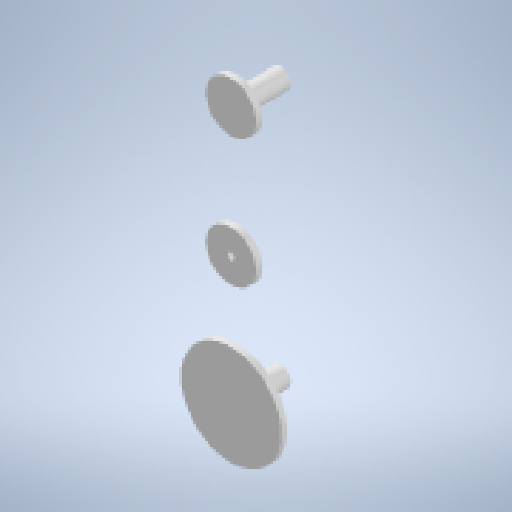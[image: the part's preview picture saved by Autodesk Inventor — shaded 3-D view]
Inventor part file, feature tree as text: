
AUTODESK INVENTOR PART (.ipt)
format: ipt  version: 2023 (Build 270158000, 158)  size: 155,136 bytes
history: native  units: mm
features: reference x4, other x4, extrude x2, sketch x1
ambient origin geometry x8: Origin, YZ Plane, XZ Plane, XY Plane, X Axis, Y Axis, Z Axis, Center Point
bodies: Solid1 (feature_tree)
feature tree (11):
  sketch  "Sketch1"  dims[d0=5.5mm d1=80.0mm d2=25.0mm d3=40.0mm d4=40.0mm d5=5.0mm d6=0.0mm d7=35.0mm d8=0.0mm]
  extrude  "Extrusion1"  Depth=35.0mm
  extrude  "Extrusion2"  Depth=35.0mm
  reference  "Reference1"
  reference  "Reference2"
  reference  "Reference3"
  reference  "Reference4"
  other  "<userpath>\OneDrive\Namizje\school\4. letnik\Matura\Izdelovanje\3D model\3D_skenner.iam"
  other  "3D_skenner.iam"
  other  "motor_sample:1"
  other  "Ogrodje_spodaj_1:1"
